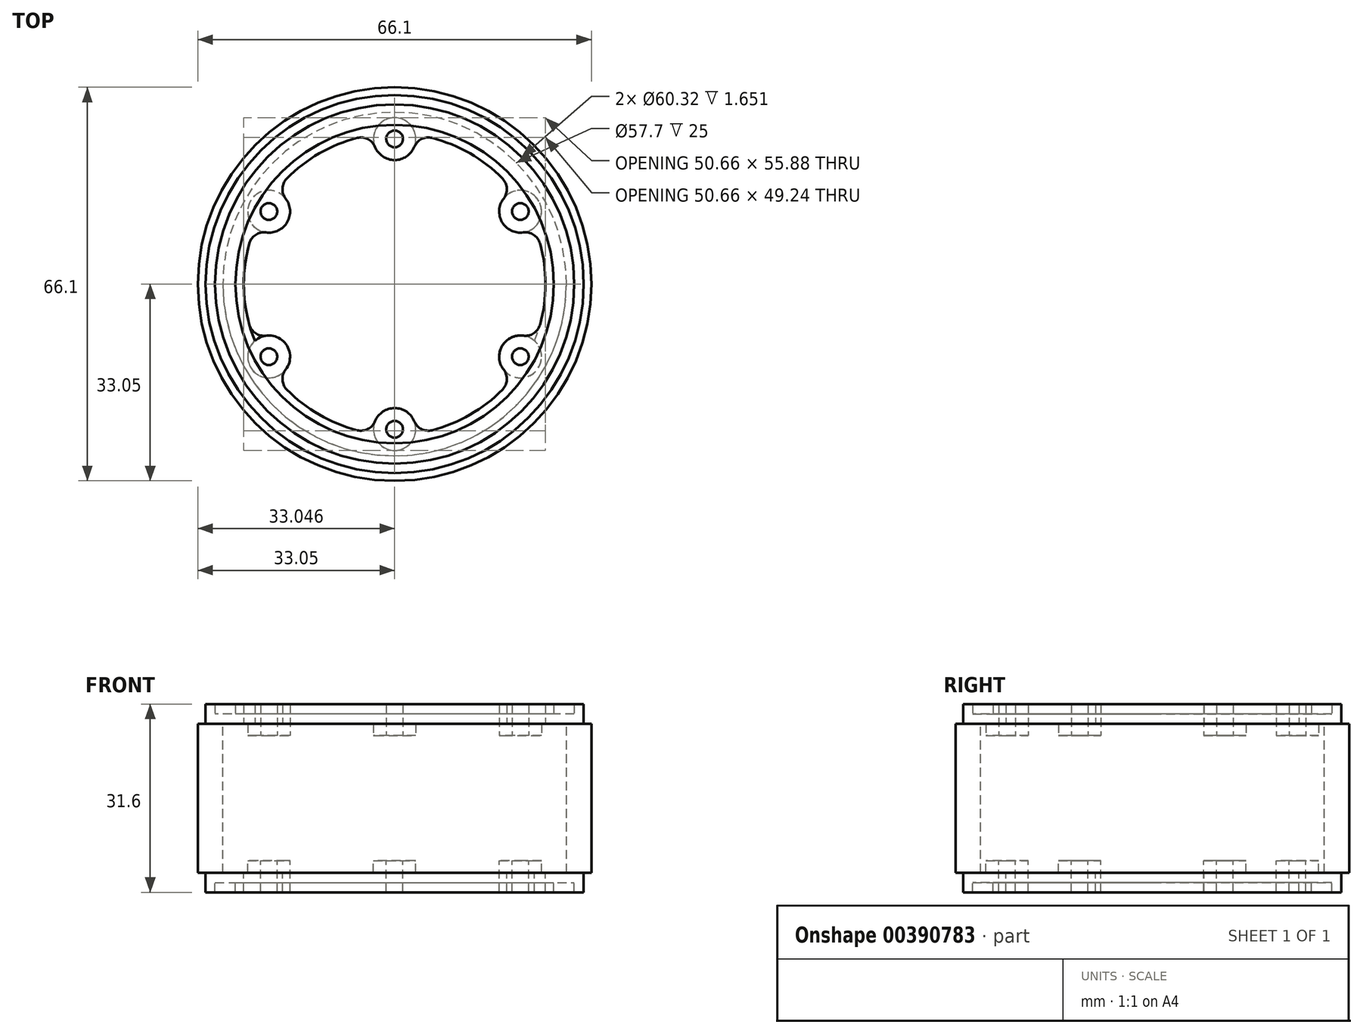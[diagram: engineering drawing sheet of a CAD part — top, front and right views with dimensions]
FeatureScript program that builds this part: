
annotation { "Feature Type Name" : "Feature", "Feature Type Description" : "" }
export const myFeature = defineFeature(function(context is Context, id is Id, definition is map)
    precondition{}
    {
        {
            var Q0;
            Q0=qCreatedBy(makeId("Top.planeOp"),FACE);
            var sketch = newSketch(context, id + "F0", { "sketchPlane" : qUnion([Q0])});
            skCircle(sketch, "E0", {"center": v(0, 0) * mm, "radius": 31.75 * mm});
            skCircle(sketch, "E1", {"center": v(0, 0) * mm, "radius": 25.34 * mm});
            skSolve(sketch);
        }
        {
            var Q0;
            Q0=makeQuery(id+"F0.imprint","IMPRINT",FACE,{"disambiguationData":[TD([[makeQuery(id+"F0.imprint","IMPRINT",EDGE,{"derivedFrom":sQuery(id+"F0.wireOp",EDGE,"E0")}),1.0]])]});
            extrude(context, id + "F1", {"entities" : qUnion([Q0]), "depth" : 1.65 * mm});
        }
        {
            var Q0;
            Q0=makeQuery(id+"F1.opExtrude","CAP_FACE",FACE,{"disambiguationData":[OSD([sQuery(id+"F0.wireOp",EDGE,"E0"),sQuery(id+"F0.wireOp",EDGE,"E1")])],"isStart":false});
            var sketch = newSketch(context, id + "F2", { "sketchPlane" : qUnion([Q0])});
            skCircle(sketch, "E2", {"center": v(0, 0) * mm, "radius": 30.16 * mm});
            skCircle(sketch, "E3", {"center": v(0, 0) * mm, "radius": 26.73 * mm});
            skSolve(sketch);
        }
        {
            var Q0;
            Q0=makeQuery(id+"F2.imprint","IMPRINT",FACE,{"disambiguationData":[TD([[makeQuery(id+"F2.imprint","IMPRINT",EDGE,{"derivedFrom":sQuery(id+"F2.wireOp",EDGE,"E2")}),-1.0]])]});
            var Q1;
            Q1=makeQuery(id+"F2.imprint","IMPRINT",FACE,{"disambiguationData":[TD([[makeQuery(id+"F2.imprint","IMPRINT",EDGE,{"derivedFrom":sQuery(id+"F2.wireOp",EDGE,"E3")}),1.0]])]});
            extrude(context, id + "F3", {"entities" : qUnion([Q0, Q1]), "operationType" : NewBodyOperationType.ADD, "depth" : 1.65 * mm});
        }
        {
            var Q0;
            Q0=makeQuery(id+"F0.imprint","IMPRINT",FACE,{"disambiguationData":[TD([[makeQuery(id+"F0.imprint","IMPRINT",EDGE,{"derivedFrom":sQuery(id+"F0.wireOp",EDGE,"E0")}),1.0]])]});
            var sketch = newSketch(context, id + "F4", { "sketchPlane" : qUnion([Q0])});
            skCircle(sketch, "E4", {"center": v(0, 0) * mm, "radius": 24.38 * mm, "construction": true});
            skCircle(sketch, "E5", {"center": v(0, 24.38) * mm, "radius": 1.4 * mm});
            skCircle(sketch, "E6.1.0", {"center": v(-21.12, 12.2) * mm, "radius": 1.4 * mm});
            skCircle(sketch, "E6.2.0", {"center": v(-21.12, -12.2) * mm, "radius": 1.4 * mm});
            skCircle(sketch, "E6.3.0", {"center": v(0, -24.38) * mm, "radius": 1.4 * mm});
            skCircle(sketch, "E6.4.0", {"center": v(21.12, -12.2) * mm, "radius": 1.4 * mm});
            skCircle(sketch, "E6.5.0", {"center": v(21.12, 12.2) * mm, "radius": 1.4 * mm});
            skCircle(sketch, "E7", {"center": v(0, 24.38) * mm, "radius": 3.56 * mm});
            skCircle(sketch, "E8.1.0", {"center": v(-21.12, 12.2) * mm, "radius": 3.56 * mm});
            skCircle(sketch, "E8.2.0", {"center": v(-21.12, -12.2) * mm, "radius": 3.56 * mm});
            skCircle(sketch, "E8.3.0", {"center": v(0, -24.38) * mm, "radius": 3.56 * mm});
            skCircle(sketch, "E8.4.0", {"center": v(21.12, -12.2) * mm, "radius": 3.56 * mm});
            skCircle(sketch, "E8.5.0", {"center": v(21.12, 12.2) * mm, "radius": 3.56 * mm});
            skSolve(sketch);
        }
        {
            var Q0;
            {var subQ0=sQuery(id+"F4.wireOp",EDGE,"E6.3.0");var subQ1=makeQuery(id+"F0.imprint","IMPRINT",EDGE,{"derivedFrom":sQuery(id+"F0.wireOp",EDGE,"E1")});var subQ2=makeQuery(id+"F4.imprint","INTERSECT",VERTEX,{"disambiguationData":[OD(0.0)],"derivedFrom":[subQ1,subQ0]});Q0=makeQuery(id+"F4.imprint","IMPRINT",FACE,{"disambiguationData":[TD([[makeQuery(id+"F4.imprint","IMPRINT",EDGE,{"disambiguationData":[TD([[subQ2,1.0]])],"derivedFrom":subQ0}),-1.0]])]});}
            var Q1;
            {var subQ0=sQuery(id+"F4.wireOp",EDGE,"E6.4.0");var subQ1=makeQuery(id+"F0.imprint","IMPRINT",EDGE,{"derivedFrom":sQuery(id+"F0.wireOp",EDGE,"E1")});var subQ2=makeQuery(id+"F4.imprint","INTERSECT",VERTEX,{"disambiguationData":[OD(0.0)],"derivedFrom":[subQ1,subQ0]});Q1=makeQuery(id+"F4.imprint","IMPRINT",FACE,{"disambiguationData":[TD([[makeQuery(id+"F4.imprint","IMPRINT",EDGE,{"disambiguationData":[TD([[subQ2,1.0]])],"derivedFrom":subQ0}),-1.0]])]});}
            var Q2;
            {var subQ0=sQuery(id+"F4.wireOp",EDGE,"E6.2.0");var subQ1=makeQuery(id+"F0.imprint","IMPRINT",EDGE,{"derivedFrom":sQuery(id+"F0.wireOp",EDGE,"E1")});var subQ2=makeQuery(id+"F4.imprint","INTERSECT",VERTEX,{"disambiguationData":[OD(0.0)],"derivedFrom":[subQ1,subQ0]});Q2=makeQuery(id+"F4.imprint","IMPRINT",FACE,{"disambiguationData":[TD([[makeQuery(id+"F4.imprint","IMPRINT",EDGE,{"disambiguationData":[TD([[subQ2,1.0]])],"derivedFrom":subQ0}),-1.0]])]});}
            var Q3;
            {var subQ0=sQuery(id+"F4.wireOp",EDGE,"E6.1.0");var subQ1=makeQuery(id+"F0.imprint","IMPRINT",EDGE,{"derivedFrom":sQuery(id+"F0.wireOp",EDGE,"E1")});var subQ2=makeQuery(id+"F4.imprint","INTERSECT",VERTEX,{"disambiguationData":[OD(0.0)],"derivedFrom":[subQ1,subQ0]});Q3=makeQuery(id+"F4.imprint","IMPRINT",FACE,{"disambiguationData":[TD([[makeQuery(id+"F4.imprint","IMPRINT",EDGE,{"disambiguationData":[TD([[subQ2,-1.0]])],"derivedFrom":subQ0}),-1.0]])]});}
            var Q4;
            {var subQ0=sQuery(id+"F4.wireOp",EDGE,"E6.5.0");var subQ1=makeQuery(id+"F0.imprint","IMPRINT",EDGE,{"derivedFrom":sQuery(id+"F0.wireOp",EDGE,"E1")});var subQ2=makeQuery(id+"F4.imprint","INTERSECT",VERTEX,{"disambiguationData":[OD(0.0)],"derivedFrom":[subQ1,subQ0]});Q4=makeQuery(id+"F4.imprint","IMPRINT",FACE,{"disambiguationData":[TD([[makeQuery(id+"F4.imprint","IMPRINT",EDGE,{"disambiguationData":[TD([[subQ2,-1.0]])],"derivedFrom":subQ0}),-1.0]])]});}
            var Q5;
            {var subQ0=sQuery(id+"F4.wireOp",EDGE,"E5");var subQ1=makeQuery(id+"F0.imprint","IMPRINT",EDGE,{"derivedFrom":sQuery(id+"F0.wireOp",EDGE,"E1")});var subQ2=makeQuery(id+"F4.imprint","INTERSECT",VERTEX,{"disambiguationData":[OD(0.0)],"derivedFrom":[subQ1,subQ0]});Q5=makeQuery(id+"F4.imprint","IMPRINT",FACE,{"disambiguationData":[TD([[makeQuery(id+"F4.imprint","IMPRINT",EDGE,{"disambiguationData":[TD([[subQ2,-1.0]])],"derivedFrom":subQ0}),-1.0]])]});}
            extrude(context, id + "F5", {"entities" : qUnion([Q0, Q1, Q2, Q3, Q4, Q5]), "operationType" : NewBodyOperationType.ADD, "depth" : 3.3 * mm});
        }
        {
            var Q0;
            {var subQ0=sQuery(id+"F4.wireOp",EDGE,"E8.1.0");var subQ1=sQuery(id+"F0.wireOp",EDGE,"E1");Q0=makeQuery(id+"F5.opExtrude","SWEPT_EDGE",EDGE,{"disambiguationData":[OSD([subQ1,subQ0]),TDD([makeQuery(id+"F4.imprint","INTERSECT",VERTEX,{"disambiguationData":[OD(0.0)],"derivedFrom":[makeQuery(id+"F0.imprint","IMPRINT",EDGE,{"derivedFrom":subQ1}),subQ0]})])]});}
            var Q1;
            {var subQ0=sQuery(id+"F4.wireOp",EDGE,"E8.1.0");var subQ1=sQuery(id+"F0.wireOp",EDGE,"E1");Q1=makeQuery(id+"F5.opExtrude","SWEPT_EDGE",EDGE,{"disambiguationData":[OSD([subQ1,subQ0]),TDD([makeQuery(id+"F4.imprint","INTERSECT",VERTEX,{"disambiguationData":[OD(1.0)],"derivedFrom":[makeQuery(id+"F0.imprint","IMPRINT",EDGE,{"derivedFrom":subQ1}),subQ0]})])]});}
            var Q2;
            {var subQ0=sQuery(id+"F4.wireOp",EDGE,"E8.2.0");var subQ1=sQuery(id+"F0.wireOp",EDGE,"E1");Q2=makeQuery(id+"F5.opExtrude","SWEPT_EDGE",EDGE,{"disambiguationData":[OSD([subQ1,subQ0]),TDD([makeQuery(id+"F4.imprint","INTERSECT",VERTEX,{"disambiguationData":[OD(1.0)],"derivedFrom":[makeQuery(id+"F0.imprint","IMPRINT",EDGE,{"derivedFrom":subQ1}),subQ0]})])]});}
            var Q3;
            {var subQ0=sQuery(id+"F4.wireOp",EDGE,"E7");var subQ1=sQuery(id+"F0.wireOp",EDGE,"E1");Q3=makeQuery(id+"F5.opExtrude","SWEPT_EDGE",EDGE,{"disambiguationData":[OSD([subQ1,subQ0]),TDD([makeQuery(id+"F4.imprint","INTERSECT",VERTEX,{"disambiguationData":[OD(1.0)],"derivedFrom":[makeQuery(id+"F0.imprint","IMPRINT",EDGE,{"derivedFrom":subQ1}),subQ0]})])]});}
            var Q4;
            {var subQ0=sQuery(id+"F4.wireOp",EDGE,"E7");var subQ1=sQuery(id+"F0.wireOp",EDGE,"E1");Q4=makeQuery(id+"F5.opExtrude","SWEPT_EDGE",EDGE,{"disambiguationData":[OSD([subQ1,subQ0]),TDD([makeQuery(id+"F4.imprint","INTERSECT",VERTEX,{"disambiguationData":[OD(0.0)],"derivedFrom":[makeQuery(id+"F0.imprint","IMPRINT",EDGE,{"derivedFrom":subQ1}),subQ0]})])]});}
            var Q5;
            {var subQ0=sQuery(id+"F4.wireOp",EDGE,"E8.5.0");var subQ1=sQuery(id+"F0.wireOp",EDGE,"E1");Q5=makeQuery(id+"F5.opExtrude","SWEPT_EDGE",EDGE,{"disambiguationData":[OSD([subQ1,subQ0]),TDD([makeQuery(id+"F4.imprint","INTERSECT",VERTEX,{"disambiguationData":[OD(0.0)],"derivedFrom":[makeQuery(id+"F0.imprint","IMPRINT",EDGE,{"derivedFrom":subQ1}),subQ0]})])]});}
            var Q6;
            {var subQ0=sQuery(id+"F4.wireOp",EDGE,"E8.5.0");var subQ1=sQuery(id+"F0.wireOp",EDGE,"E1");Q6=makeQuery(id+"F5.opExtrude","SWEPT_EDGE",EDGE,{"disambiguationData":[OSD([subQ1,subQ0]),TDD([makeQuery(id+"F4.imprint","INTERSECT",VERTEX,{"disambiguationData":[OD(1.0)],"derivedFrom":[makeQuery(id+"F0.imprint","IMPRINT",EDGE,{"derivedFrom":subQ1}),subQ0]})])]});}
            var Q7;
            {var subQ0=sQuery(id+"F4.wireOp",EDGE,"E8.3.0");var subQ1=sQuery(id+"F0.wireOp",EDGE,"E1");Q7=makeQuery(id+"F5.opExtrude","SWEPT_EDGE",EDGE,{"disambiguationData":[OSD([subQ1,subQ0]),TDD([makeQuery(id+"F4.imprint","INTERSECT",VERTEX,{"disambiguationData":[OD(1.0)],"derivedFrom":[makeQuery(id+"F0.imprint","IMPRINT",EDGE,{"derivedFrom":subQ1}),subQ0]})])]});}
            var Q8;
            {var subQ0=sQuery(id+"F4.wireOp",EDGE,"E8.3.0");var subQ1=sQuery(id+"F0.wireOp",EDGE,"E1");Q8=makeQuery(id+"F5.opExtrude","SWEPT_EDGE",EDGE,{"disambiguationData":[OSD([subQ1,subQ0]),TDD([makeQuery(id+"F4.imprint","INTERSECT",VERTEX,{"disambiguationData":[OD(0.0)],"derivedFrom":[makeQuery(id+"F0.imprint","IMPRINT",EDGE,{"derivedFrom":subQ1}),subQ0]})])]});}
            var Q9;
            {var subQ0=sQuery(id+"F4.wireOp",EDGE,"E8.4.0");var subQ1=sQuery(id+"F0.wireOp",EDGE,"E1");Q9=makeQuery(id+"F5.opExtrude","SWEPT_EDGE",EDGE,{"disambiguationData":[OSD([subQ1,subQ0]),TDD([makeQuery(id+"F4.imprint","INTERSECT",VERTEX,{"disambiguationData":[OD(1.0)],"derivedFrom":[makeQuery(id+"F0.imprint","IMPRINT",EDGE,{"derivedFrom":subQ1}),subQ0]})])]});}
            var Q10;
            {var subQ0=sQuery(id+"F4.wireOp",EDGE,"E8.4.0");var subQ1=sQuery(id+"F0.wireOp",EDGE,"E1");Q10=makeQuery(id+"F5.opExtrude","SWEPT_EDGE",EDGE,{"disambiguationData":[OSD([subQ1,subQ0]),TDD([makeQuery(id+"F4.imprint","INTERSECT",VERTEX,{"disambiguationData":[OD(0.0)],"derivedFrom":[makeQuery(id+"F0.imprint","IMPRINT",EDGE,{"derivedFrom":subQ1}),subQ0]})])]});}
            fillet(context, id + "F6", {"entities" : qUnion([Q0, Q1, Q2, Q3, Q4, Q5, Q6, Q7, Q8, Q9, Q10]), "radius" : 2.54 * mm, "tangentPropagation" : true, "allowEdgeOverflow" : false});
        }
        {
            var Q0;
            {var subQ0=sQuery(id+"F4.wireOp",EDGE,"E5");var subQ1=makeQuery(id+"F0.imprint","IMPRINT",EDGE,{"derivedFrom":sQuery(id+"F0.wireOp",EDGE,"E1")});var subQ2=makeQuery(id+"F4.imprint","INTERSECT",VERTEX,{"disambiguationData":[OD(0.0)],"derivedFrom":[subQ1,subQ0]});Q0=makeQuery(id+"F4.imprint","IMPRINT",FACE,{"disambiguationData":[TD([[makeQuery(id+"F4.imprint","IMPRINT",EDGE,{"disambiguationData":[TD([[subQ2,1.0]])],"derivedFrom":subQ0}),1.0]])]});}
            var Q1;
            {var subQ0=sQuery(id+"F4.wireOp",EDGE,"E6.5.0");var subQ1=makeQuery(id+"F0.imprint","IMPRINT",EDGE,{"derivedFrom":sQuery(id+"F0.wireOp",EDGE,"E1")});var subQ2=makeQuery(id+"F4.imprint","INTERSECT",VERTEX,{"disambiguationData":[OD(0.0)],"derivedFrom":[subQ1,subQ0]});Q1=makeQuery(id+"F4.imprint","IMPRINT",FACE,{"disambiguationData":[TD([[makeQuery(id+"F4.imprint","IMPRINT",EDGE,{"disambiguationData":[TD([[subQ2,1.0]])],"derivedFrom":subQ0}),1.0]])]});}
            var Q2;
            {var subQ0=sQuery(id+"F4.wireOp",EDGE,"E6.4.0");var subQ1=makeQuery(id+"F0.imprint","IMPRINT",EDGE,{"derivedFrom":sQuery(id+"F0.wireOp",EDGE,"E1")});var subQ2=makeQuery(id+"F4.imprint","INTERSECT",VERTEX,{"disambiguationData":[OD(0.0)],"derivedFrom":[subQ1,subQ0]});Q2=makeQuery(id+"F4.imprint","IMPRINT",FACE,{"disambiguationData":[TD([[makeQuery(id+"F4.imprint","IMPRINT",EDGE,{"disambiguationData":[TD([[subQ2,-1.0]])],"derivedFrom":subQ0}),1.0]])]});}
            var Q3;
            {var subQ0=sQuery(id+"F4.wireOp",EDGE,"E6.3.0");var subQ1=makeQuery(id+"F0.imprint","IMPRINT",EDGE,{"derivedFrom":sQuery(id+"F0.wireOp",EDGE,"E1")});var subQ2=makeQuery(id+"F4.imprint","INTERSECT",VERTEX,{"disambiguationData":[OD(0.0)],"derivedFrom":[subQ1,subQ0]});Q3=makeQuery(id+"F4.imprint","IMPRINT",FACE,{"disambiguationData":[TD([[makeQuery(id+"F4.imprint","IMPRINT",EDGE,{"disambiguationData":[TD([[subQ2,-1.0]])],"derivedFrom":subQ0}),1.0]])]});}
            var Q4;
            {var subQ0=sQuery(id+"F4.wireOp",EDGE,"E6.1.0");var subQ1=makeQuery(id+"F0.imprint","IMPRINT",EDGE,{"derivedFrom":sQuery(id+"F0.wireOp",EDGE,"E1")});var subQ2=makeQuery(id+"F4.imprint","INTERSECT",VERTEX,{"disambiguationData":[OD(0.0)],"derivedFrom":[subQ1,subQ0]});Q4=makeQuery(id+"F4.imprint","IMPRINT",FACE,{"disambiguationData":[TD([[makeQuery(id+"F4.imprint","IMPRINT",EDGE,{"disambiguationData":[TD([[subQ2,1.0]])],"derivedFrom":subQ0}),1.0]])]});}
            var Q5;
            {var subQ0=sQuery(id+"F4.wireOp",EDGE,"E6.2.0");var subQ1=makeQuery(id+"F0.imprint","IMPRINT",EDGE,{"derivedFrom":sQuery(id+"F0.wireOp",EDGE,"E1")});var subQ2=makeQuery(id+"F4.imprint","INTERSECT",VERTEX,{"disambiguationData":[OD(0.0)],"derivedFrom":[subQ1,subQ0]});Q5=makeQuery(id+"F4.imprint","IMPRINT",FACE,{"disambiguationData":[TD([[makeQuery(id+"F4.imprint","IMPRINT",EDGE,{"disambiguationData":[TD([[subQ2,-1.0]])],"derivedFrom":subQ0}),1.0]])]});}
            extrude(context, id + "F7", {"entities" : qUnion([Q0, Q1, Q2, Q3, Q4, Q5]), "operationType" : NewBodyOperationType.REMOVE, "depth" : 25.4 * mm});
        }
        {
            var Q0;
            Q0=makeQuery(id+"F4.imprint","IMPRINT",FACE,{"disambiguationData":[TD([[makeQuery(id+"F4.imprint","IMPRINT",EDGE,{"derivedFrom":makeQuery(id+"F0.imprint","IMPRINT",EDGE,{"derivedFrom":sQuery(id+"F0.wireOp",EDGE,"E0")})}),1.0]])]});
            var sketch = newSketch(context, id + "F8", { "sketchPlane" : qUnion([Q0])});
            skCircle(sketch, "E9", {"center": v(0, 0) * mm, "radius": 28.85 * mm});
            skCircle(sketch, "E10", {"center": v(0, 0) * mm, "radius": 33.05 * mm});
            skSolve(sketch);
        }
        {
            var Q0;
            Q0 = qSketchRegion(id + "F8", true);
            extrude(context, id + "F9", {"entities" : qUnion([Q0]), "oppositeDirection" : true, "depth" : 12.5 * mm});
        }
        {
            var Q0;
            Q0=makeQuery(id+"F9.opExtrude","CAP_FACE",FACE,{"disambiguationData":[OSD([sQuery(id+"F8.wireOp",EDGE,"E9"),sQuery(id+"F8.wireOp",EDGE,"E10")])],"isStart":false});
            var sketch = newSketch(context, id + "F10", { "sketchPlane" : qUnion([Q0])});
            skLineSegment(sketch, "E11", {"start": v(0, 0) * mm, "end": v(0, -41.8) * mm, "construction": true});
            skSolve(sketch);
        }
        {
            var Q0;
            Q0 = qSketchRegion(id + "F4", true);
            extrude(context, id + "F11", {"entities" : qUnion([Q0]), "operationType" : NewBodyOperationType.ADD, "oppositeDirection" : true, "depth" : 2 * mm});
        }
        {
            var Q0;
            Q0=makeQuery(id+"F9.opExtrude","CAP_FACE",FACE,{"disambiguationData":[OSD([sQuery(id+"F8.wireOp",EDGE,"E9"),sQuery(id+"F8.wireOp",EDGE,"E10")])],"isStart":false});
            var sketch = newSketch(context, id + "F12", { "sketchPlane" : qUnion([Q0])});
            skCircle(sketch, "E12", {"center": v(0, 0) * mm, "radius": 33.05 * mm});
            skCircle(sketch, "E13", {"center": v(0, 0) * mm, "radius": 28.85 * mm});
            skSolve(sketch);
        }
        {
            var Q0;
            Q0=makeQuery(id+"F1.opExtrude","SWEPT_BODY",BODY,{"disambiguationData":[OSD([sQuery(id+"F0.wireOp",EDGE,"E0"),sQuery(id+"F0.wireOp",EDGE,"E1")])]});
            var Q1;
            Q1=sQuery(id+"F10.wireOp",EDGE,"E11");
            transform(context, id + "F13", {"entities" : qUnion([Q0]), "transformType" : TransformType.ROTATION, "transformAxis" : qUnion([Q1]), "angle" : 180 * degree, "makeCopy" : true});
        }
        {
            var Q0;
            Q0 = qSketchRegion(id + "F12", true);
            extrude(context, id + "F14", {"entities" : qUnion([Q0]), "operationType" : NewBodyOperationType.ADD, "depth" : 12.5 * mm});
        }
    });
